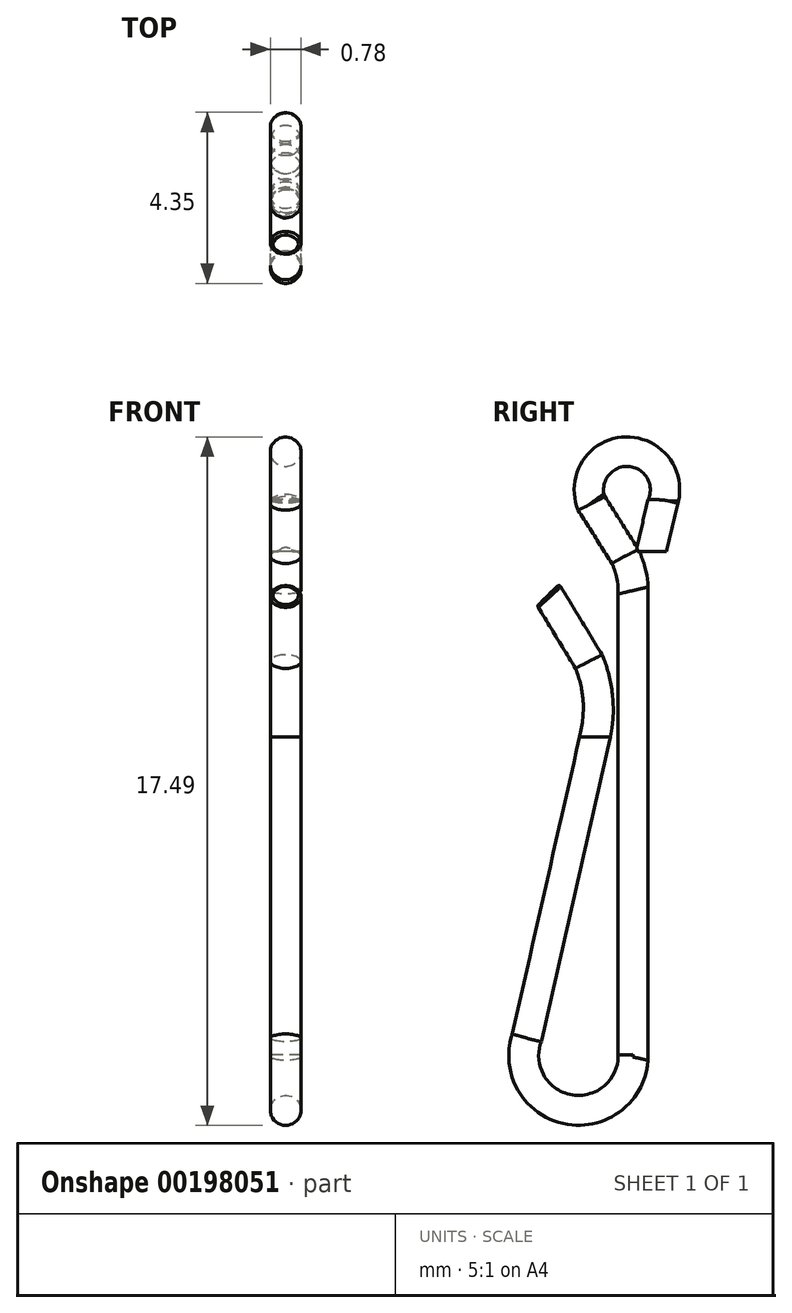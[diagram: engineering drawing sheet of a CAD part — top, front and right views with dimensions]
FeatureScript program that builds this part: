
annotation { "Feature Type Name" : "Feature", "Feature Type Description" : "" }
export const myFeature = defineFeature(function(context is Context, id is Id, definition is map)
    precondition{}
    {
        {
            var Q0;
            Q0=qCreatedBy(makeId("Top.planeOp"),FACE);
            cPlane(context, id + "F0", {"entities" : qUnion([Q0]), "cplaneType" : CPlaneType.OFFSET, "offset" : 4.4 * mm, "oppositeDirection" : true, "width" : 150 * mm, "height" : 150 * mm});
        }
        {
            var Q0;
            Q0=qCreatedBy(makeId("Right.planeOp"),FACE);
            var sketch = newSketch(context, id + "F1", { "sketchPlane" : qUnion([Q0])});
            skLineSegment(sketch, "E0", {"start": v(0, -6.12) * mm, "end": v(0, -25.74) * mm});
            skLineSegment(sketch, "E1", {"start": v(-4.11, -25.08) * mm, "end": v(-1.2, -12.27) * mm});
            skArc(sketch, "E2", {"start": v(-4.11, -25.08) * mm, "mid": v(-2.45, -27.85) * mm, "end": v(0, -25.74) * mm});
            skLineSegment(sketch, "E3", {"start": v(-1.5, -8.98) * mm, "end": v(-3.24, -6.12) * mm});
            skArc(sketch, "E4", {"start": v(-1.2, -12.27) * mm, "mid": v(-1.1, -10.6) * mm, "end": v(-1.5, -8.98) * mm});
            skLineSegment(sketch, "E5", {"start": v(-0.32, -4.71) * mm, "end": v(-1.73, -2.47) * mm});
            skPoint(sketch, "E5.endSnap0", {"position": v(-2.37, -7.55) * mm});
            skArc(sketch, "E6", {"start": v(0, -6.12) * mm, "mid": v(-0.08, -5.4) * mm, "end": v(-0.32, -4.71) * mm});
            skLineSegment(sketch, "E7", {"start": v(1.17, -4.4) * mm, "end": v(1.68, -2.27) * mm});
            skArc(sketch, "E8", {"start": v(1.68, -2.27) * mm, "mid": v(-0.17, 0) * mm, "end": v(-1.73, -2.47) * mm});
            skSolve(sketch);
        }
        {
            var Q0;
            Q0=qCreatedBy(id+"F0.planeOp",FACE);
            var sketch = newSketch(context, id + "F2", { "sketchPlane" : qUnion([Q0])});
            skCircle(sketch, "E9", {"center": v(0, 0.97) * mm, "radius": 0.65 * mm});
            skSolve(sketch);
        }
        {
            var Q0;
            Q0=makeQuery(id+"F2.imprint","IMPRINT",FACE,{"disambiguationData":[TD([[makeQuery(id+"F2.imprint","IMPRINT",EDGE,{"derivedFrom":sQuery(id+"F2.wireOp",EDGE,"E9")}),1.0]])]});
            var Q1;
            Q1=sQuery(id+"F1.wireOp",EDGE,"E7");
            var Q2;
            Q2=sQuery(id+"F1.wireOp",EDGE,"E8");
            var Q3;
            Q3=sQuery(id+"F1.wireOp",EDGE,"E5");
            var Q4;
            Q4=sQuery(id+"F1.wireOp",EDGE,"E0");
            var Q5;
            Q5=sQuery(id+"F1.wireOp",EDGE,"E6");
            var Q6;
            Q6=sQuery(id+"F1.wireOp",EDGE,"E2");
            var Q7;
            Q7=sQuery(id+"F1.wireOp",EDGE,"E1");
            var Q8;
            Q8=sQuery(id+"F1.wireOp",EDGE,"E4");
            var Q9;
            Q9=sQuery(id+"F1.wireOp",EDGE,"E3");
            sweep(context, id + "F3", {"profiles" : qUnion([Q0]), "path" : qUnion([Q1, Q2, Q3, Q4, Q5, Q6, Q7, Q8, Q9])});
        }
        {
            var Q0;
            Q0=makeQuery(id+"F3.opSweep","CAP_EDGE",EDGE,{"disambiguationData":[OSD([sQuery(id+"F1.wireOp",VERTEX,"E3.end"),sQuery(id+"F2.wireOp",EDGE,"E9")])],"isStart":false});
            var Q1;
            Q1=makeQuery(id+"F3.opSweep","MID_CAP_EDGE",EDGE,{"disambiguationData":[OSD([sQuery(id+"F1.wireOp",VERTEX,"E7.start"),sQuery(id+"F2.wireOp",EDGE,"E9")])],"capPos":0.0});
            fillet(context, id + "F4", {"entities" : qUnion([Q0, Q1]), "radius" : .1 * mm, "tangentPropagation" : true, "allowEdgeOverflow" : false});
        }
        {
            var Q0;
            Q0=makeQuery(id+"F3.opSweep","SWEPT_BODY",BODY,{"disambiguationData":[OSD([sQuery(id+"F1.wireOp",EDGE,"E7"),sQuery(id+"F2.wireOp",EDGE,"E9")])]});
            var Q1;
            Q1=qCreatedBy(makeId("Origin.pointOp"),VERTEX);
            transform(context, id + "F5", {"entities" : qUnion([Q0]), "transformType" : TransformType.SCALE_UNIFORMLY, "scale" : 0.6, "scalePoint" : qUnion([Q1]), "makeCopy" : false});
        }
    });
